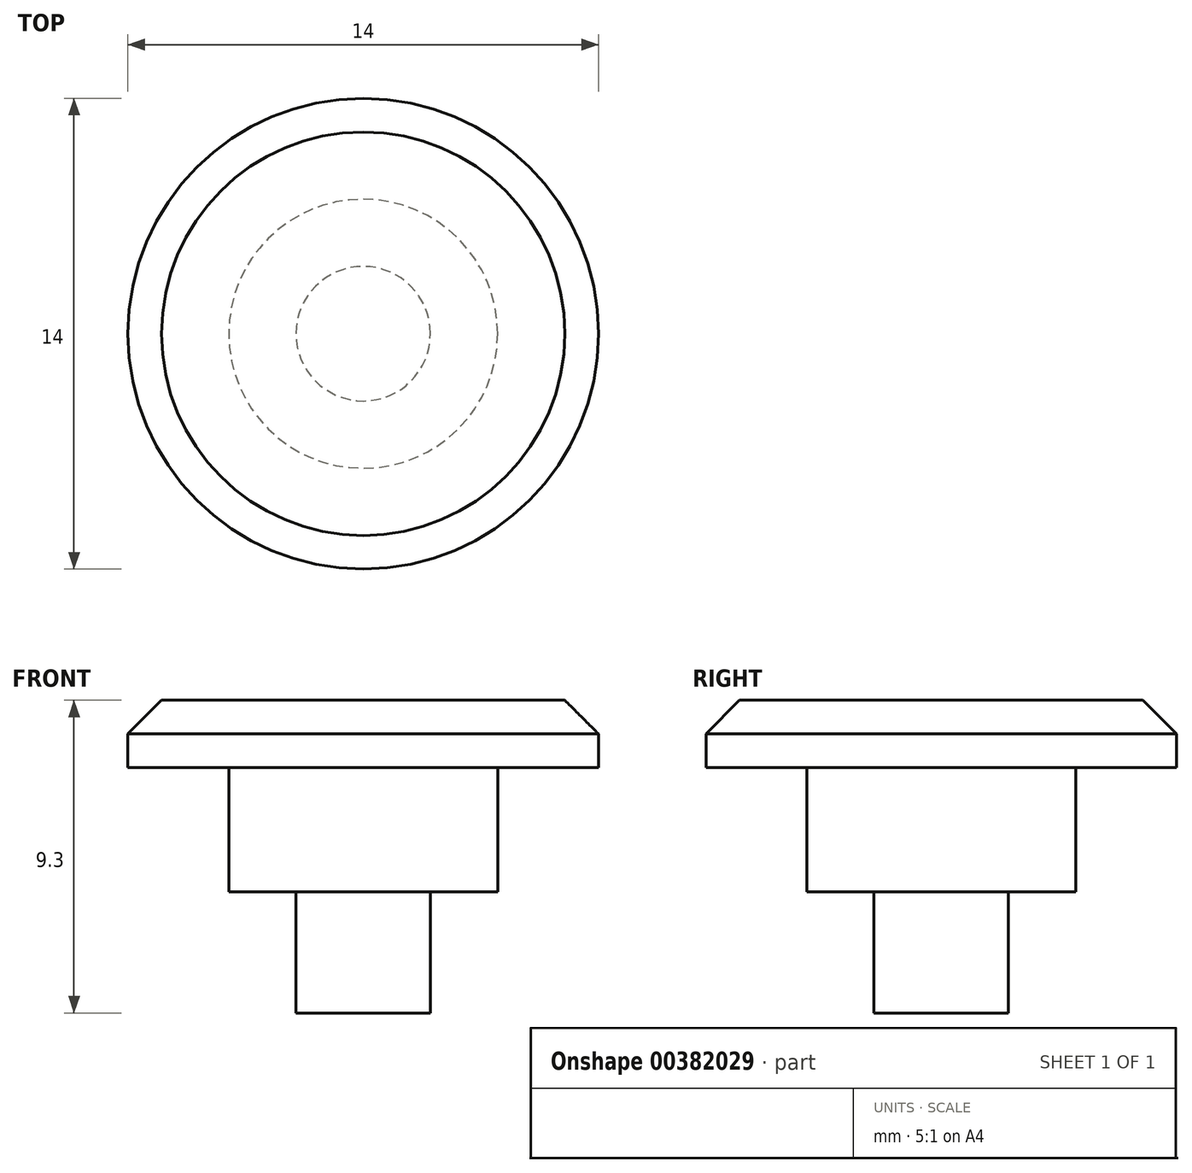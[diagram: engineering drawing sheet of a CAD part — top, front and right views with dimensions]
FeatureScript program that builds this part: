
annotation { "Feature Type Name" : "Feature", "Feature Type Description" : "" }
export const myFeature = defineFeature(function(context is Context, id is Id, definition is map)
    precondition{}
    {
        {
            var Q0;
            Q0=qCreatedBy(makeId("Top.planeOp"),FACE);
            var sketch = newSketch(context, id + "F0", { "sketchPlane" : qUnion([Q0])});
            skCircle(sketch, "E0", {"center": v(0, 0) * mm, "radius": 2 * mm});
            skCircle(sketch, "E1", {"center": v(0, 0) * mm, "radius": 4 * mm});
            skCircle(sketch, "E2", {"center": v(0, 0) * mm, "radius": 7 * mm});
            skSolve(sketch);
        }
        {
            var Q0;
            Q0=makeQuery(id+"F0.imprint","IMPRINT",FACE,{"disambiguationData":[TD([[makeQuery(id+"F0.imprint","IMPRINT",EDGE,{"derivedFrom":sQuery(id+"F0.wireOp",EDGE,"E1")}),-1.0]])]});
            var Q1;
            Q1=makeQuery(id+"F0.imprint","IMPRINT",FACE,{"disambiguationData":[TD([[makeQuery(id+"F0.imprint","IMPRINT",EDGE,{"derivedFrom":sQuery(id+"F0.wireOp",EDGE,"E0")}),-1.0]])]});
            var Q2;
            Q2=makeQuery(id+"F0.imprint","IMPRINT",FACE,{"disambiguationData":[TD([[makeQuery(id+"F0.imprint","IMPRINT",EDGE,{"derivedFrom":sQuery(id+"F0.wireOp",EDGE,"E0")}),1.0]])]});
            extrude(context, id + "F1", {"entities" : qUnion([Q0, Q1, Q2]), "depth" : 2 * mm});
        }
        {
            var Q0;
            Q0=makeQuery(id+"F1.opExtrude","CAP_FACE",FACE,{"disambiguationData":[OSD([sQuery(id+"F0.wireOp",EDGE,"E2")])],"isStart":false});
            chamfer(context, id + "F2", {"entities" : qUnion([Q0]), "width" : 1 * mm, "tangentPropagation" : true});
        }
        {
            var Q0;
            Q0=makeQuery(id+"F0.imprint","IMPRINT",FACE,{"disambiguationData":[TD([[makeQuery(id+"F0.imprint","IMPRINT",EDGE,{"derivedFrom":sQuery(id+"F0.wireOp",EDGE,"E0")}),1.0]])]});
            extrude(context, id + "F3", {"entities" : qUnion([Q0]), "operationType" : NewBodyOperationType.ADD, "depth" : -7.3 * mm});
        }
        {
            var Q0;
            Q0=makeQuery(id+"F0.imprint","IMPRINT",FACE,{"disambiguationData":[TD([[makeQuery(id+"F0.imprint","IMPRINT",EDGE,{"derivedFrom":sQuery(id+"F0.wireOp",EDGE,"E0")}),-1.0]])]});
            extrude(context, id + "F4", {"entities" : qUnion([Q0]), "operationType" : NewBodyOperationType.ADD, "depth" : -3.7 * mm});
        }
    });
